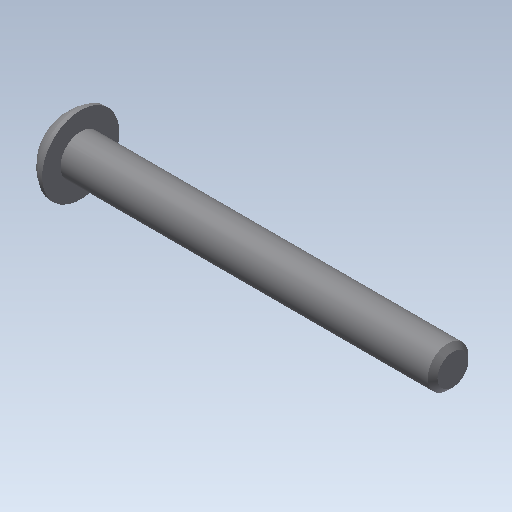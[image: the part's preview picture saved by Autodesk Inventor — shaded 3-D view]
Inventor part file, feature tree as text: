
AUTODESK INVENTOR PART (.ipt)
format: ipt  version: 2020 (Build 240168000, 168)  size: 129,024 bytes
history: native  units: in
note: dims shown in document units (in); Inventor stores cm internally (conversion verified against a paired STEP export)
features: other x3, extrude x1, chamfer x1, imported_body x1, sketch x1
ambient origin geometry x8: Origin, YZ Plane, XZ Plane, XY Plane, X Axis, Y Axis, Z Axis, Center Point
bodies: Body1 (feature_tree)
feature tree (7):
  other  "Bolt 1.5 inch"
  parser-record x1  (decoder bookkeeping rows leaked as tree rows — omitted from the tree; the rows remain in map.json)
  other  "Bolt"
  extrude  "thread length"  Depth=1.5in TaperAngle=0.0deg
  chamfer  "thread chamfer"  Distance=0.02in Angle=45.0deg
  imported_body  "Base1"
  sketch  "Sketch1"  dims[d0=0.164in d1=1.5in d2=0.0in d3=0.02in d4=0.125in d5=45.0deg d7=0.0in d9=0.0in]
